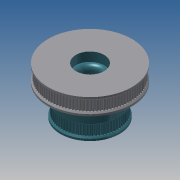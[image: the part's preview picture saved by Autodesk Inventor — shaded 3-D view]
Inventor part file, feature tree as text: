
AUTODESK INVENTOR PART (.ipt)
format: ipt  version: 2013 (Build 170138000, 138)  size: 1,208,832 bytes
history: native  units: mm
features: extrude x10, sketch x10, other x3, fillet x3, pattern_circular x1, chamfer x1
ambient origin geometry x8: Origin, YZ Plane, XZ Plane, XY Plane, X Axis, Y Axis, Z Axis, Center Point
bodies: Solid1 (feature_tree)
feature tree (28):
  other  "z idler pulley 2.iam"
  other  "100 pulley blank.ipt:1"
  other  "100 pulley blank.ipt:2"
  extrude  "Extrusion1"  Depth=10.0mm TaperAngle=0.0deg
  extrude  "Extrusion2"  Depth=10.0mm TaperAngle=0.0deg
  extrude  "Extrusion3"  Depth=7.0mm TaperAngle=0.0deg
  extrude  "Extrusion4"  Depth=7.0mm TaperAngle=0.0deg
  fillet  "Fillet1"  Radius=3.5mm
  fillet  "Fillet2"  Radius=3.5mm
  extrude  "Extrusion5"  Depth=44.055384mm
  extrude  "Extrusion6"  Depth=1.59mm
  extrude  "Extrusion7"  Depth=700.0mm TaperAngle=360.0deg
  pattern_circular  "Circular Pattern1"  Angle=45.0deg  [1 undecoded]
  extrude  "Extrusion8"  Depth=22.0mm
  extrude  "Extrusion9"  Depth=7.0mm TaperAngle=0.0deg
  chamfer  "Chamfer1"  Distance=3.5mm
  extrude  "Extrusion10"  [1 undecoded]
  fillet  "Fillet3"  [1 undecoded]
  sketch  "Sketch1"  dims[d0=10.0mm d1=10.0mm d2=0.0mm]
  sketch  "Sketch2"  dims[d3=15.0mm d5=10.0mm d6=0.0mm]
  sketch  "Sketch3"  dims[d7=22.0mm d9=7.0mm d10=0.0mm]
  sketch  "Sketch4"  dims[d11=22.0mm d13=7.0mm d14=0.0mm d15=3.5mm d16=3.5mm]
  sketch  "Sketch5"  dims[d17=29.6mm d18=0.0mm d19=44.055384mm]
  sketch  "Sketch6"  dims[d21=23.4mm d22=0.0mm d23=1.59mm]
  sketch  "Sketch7"  dims[d25=23.4mm d26=0.0mm d27=700.0mm d28=360.0deg]
  sketch  "Sketch8"  dims[d30=1.0mm]
  sketch  "Sketch9"  dims[d31=12.9mm d32=0.0mm]
  sketch  "Sketch10"  dims[d33=2.5mm d34=0.0mm d35=1.0mm d36=2.0mm d37=45.0deg d38=22.0mm d40=7.0mm d41=0.0mm d42=3.5mm]
note: 3 required parameter values undecoded (feature->parameter linkage not recoverable at this tier; creation-order binding heuristic only, values carry confidence <= 0.55)
